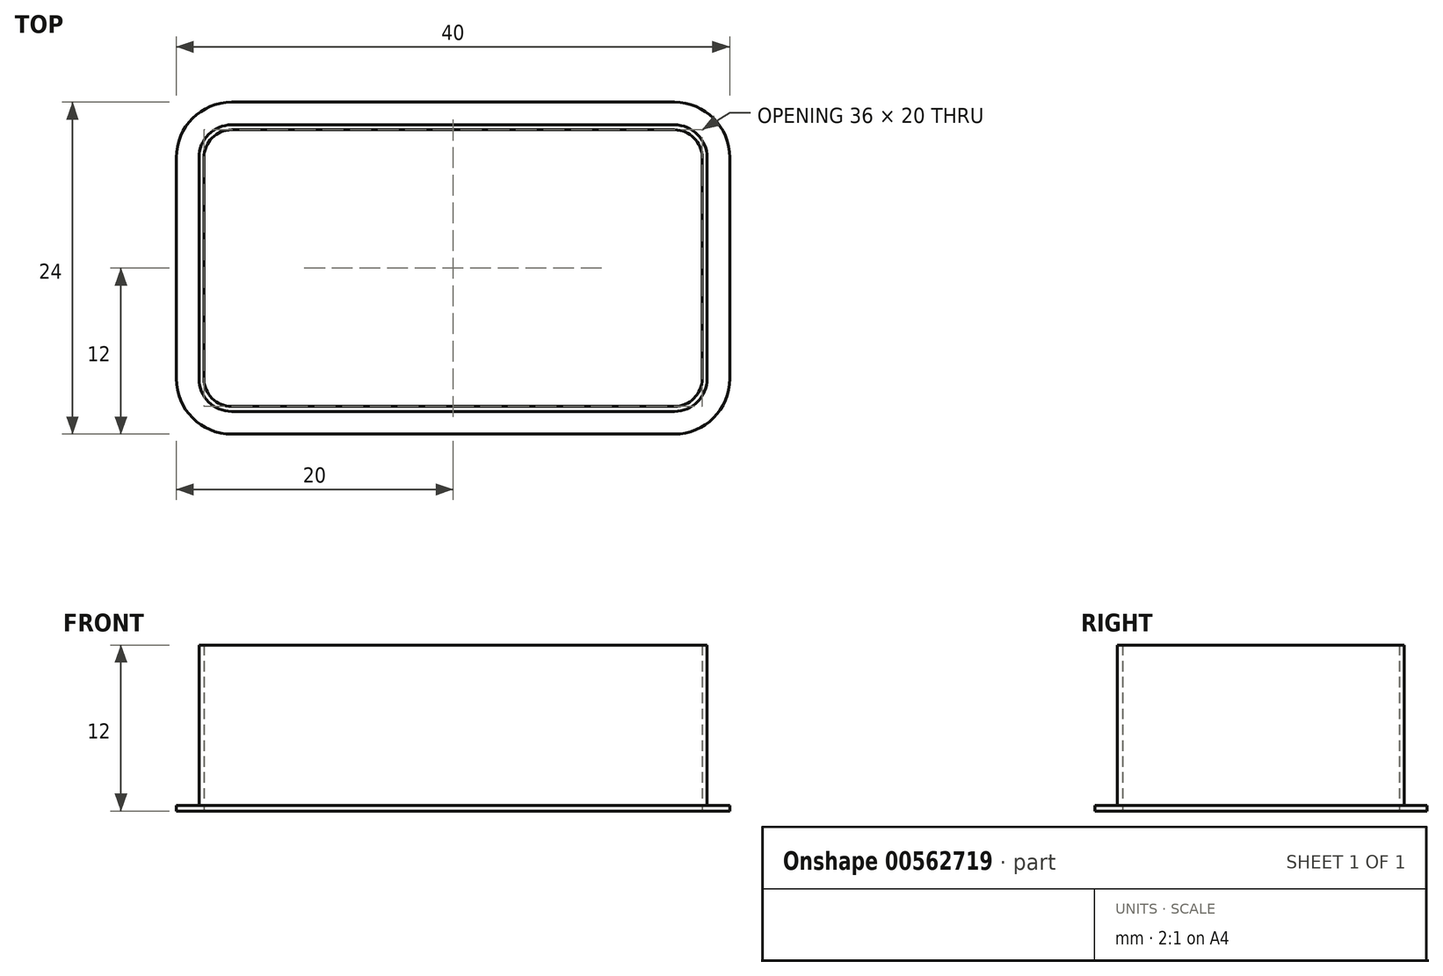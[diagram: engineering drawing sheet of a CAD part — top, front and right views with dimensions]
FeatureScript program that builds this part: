
annotation { "Feature Type Name" : "Feature", "Feature Type Description" : "" }
export const myFeature = defineFeature(function(context is Context, id is Id, definition is map)
    precondition{}
    {
        {
            var Q0;
            Q0=qCreatedBy(makeId("Top.planeOp"),FACE);
            var sketch = newSketch(context, id + "F0", { "sketchPlane" : qUnion([Q0])});
            skLineSegment(sketch, "E0.bottom", {"start": v(16, -10) * mm, "end": v(-16, -10) * mm});
            skLineSegment(sketch, "E0.top", {"start": v(16, 10) * mm, "end": v(-16, 10) * mm});
            skLineSegment(sketch, "E0.left", {"start": v(18, -8) * mm, "end": v(18, 8) * mm});
            skLineSegment(sketch, "E0.right", {"start": v(-18, -8) * mm, "end": v(-18, 8) * mm});
            skPoint(sketch, "E0.middle", {"position": v(0, 0) * mm});
            skPoint(sketch, "E1.visualSharp", {"position": v(18, 10) * mm});
            skArc(sketch, "E1.filletArc", {"start": v(18, 8) * mm, "mid": v(17.41, 9.41) * mm, "end": v(16, 10) * mm});
            skPoint(sketch, "E2.visualSharp", {"position": v(18, -10) * mm});
            skArc(sketch, "E2.filletArc", {"start": v(16, -10) * mm, "mid": v(17.41, -9.41) * mm, "end": v(18, -8) * mm});
            skPoint(sketch, "E3.visualSharp", {"position": v(-18, -10) * mm});
            skArc(sketch, "E3.filletArc", {"start": v(-18, -8) * mm, "mid": v(-17.41, -9.41) * mm, "end": v(-16, -10) * mm});
            skPoint(sketch, "E4.visualSharp", {"position": v(-18, 10) * mm});
            skArc(sketch, "E4.filletArc", {"start": v(-16, 10) * mm, "mid": v(-17.41, 9.41) * mm, "end": v(-18, 8) * mm});
            skArc(sketch, "E5.0", {"start": v(-18.36, -8) * mm, "mid": v(-17.67, -9.67) * mm, "end": v(-16, -10.36) * mm});
            skLineSegment(sketch, "E5.1", {"start": v(16, -10.36) * mm, "end": v(-16, -10.36) * mm});
            skLineSegment(sketch, "E5.2", {"start": v(-18.36, -8) * mm, "end": v(-18.36, 8) * mm});
            skArc(sketch, "E5.3", {"start": v(16, -10.36) * mm, "mid": v(17.67, -9.67) * mm, "end": v(18.36, -8) * mm});
            skArc(sketch, "E5.4", {"start": v(-16, 10.36) * mm, "mid": v(-17.67, 9.67) * mm, "end": v(-18.36, 8) * mm});
            skLineSegment(sketch, "E5.5", {"start": v(16, 10.36) * mm, "end": v(-16, 10.36) * mm});
            skArc(sketch, "E5.6", {"start": v(18.36, 8) * mm, "mid": v(17.67, 9.67) * mm, "end": v(16, 10.36) * mm});
            skLineSegment(sketch, "E5.7", {"start": v(18.36, -8) * mm, "end": v(18.36, 8) * mm});
            skArc(sketch, "E6.0", {"start": v(-20, -8) * mm, "mid": v(-18.83, -10.83) * mm, "end": v(-16, -12) * mm});
            skLineSegment(sketch, "E6.1", {"start": v(16, -12) * mm, "end": v(-16, -12) * mm});
            skLineSegment(sketch, "E6.2", {"start": v(-20, -8) * mm, "end": v(-20, 8) * mm});
            skArc(sketch, "E6.3", {"start": v(16, -12) * mm, "mid": v(18.83, -10.83) * mm, "end": v(20, -8) * mm});
            skArc(sketch, "E6.4", {"start": v(-16, 12) * mm, "mid": v(-18.83, 10.83) * mm, "end": v(-20, 8) * mm});
            skLineSegment(sketch, "E6.5", {"start": v(16, 12) * mm, "end": v(-16, 12) * mm});
            skArc(sketch, "E6.6", {"start": v(20, 8) * mm, "mid": v(18.83, 10.83) * mm, "end": v(16, 12) * mm});
            skLineSegment(sketch, "E6.7", {"start": v(20, -8) * mm, "end": v(20, 8) * mm});
            skSolve(sketch);
        }
        {
            var Q0;
            Q0=makeQuery(id+"F0.imprint","IMPRINT",FACE,{"disambiguationData":[TD([[makeQuery(id+"F0.imprint","IMPRINT",EDGE,{"derivedFrom":sQuery(id+"F0.wireOp",EDGE,"E0.bottom")}),1.0]])]});
            extrude(context, id + "F1", {"entities" : qUnion([Q0]), "depth" : 12 * mm, "offsetDistance" : 25 * mm});
        }
        {
            var Q0;
            Q0=makeQuery(id+"F0.imprint","IMPRINT",FACE,{"disambiguationData":[TD([[makeQuery(id+"F0.imprint","IMPRINT",EDGE,{"derivedFrom":sQuery(id+"F0.wireOp",EDGE,"E5.0")}),-1.0]])]});
            extrude(context, id + "F2", {"entities" : qUnion([Q0]), "operationType" : NewBodyOperationType.ADD, "depth" : 0.4 * mm, "offsetDistance" : 25 * mm});
        }
    });
